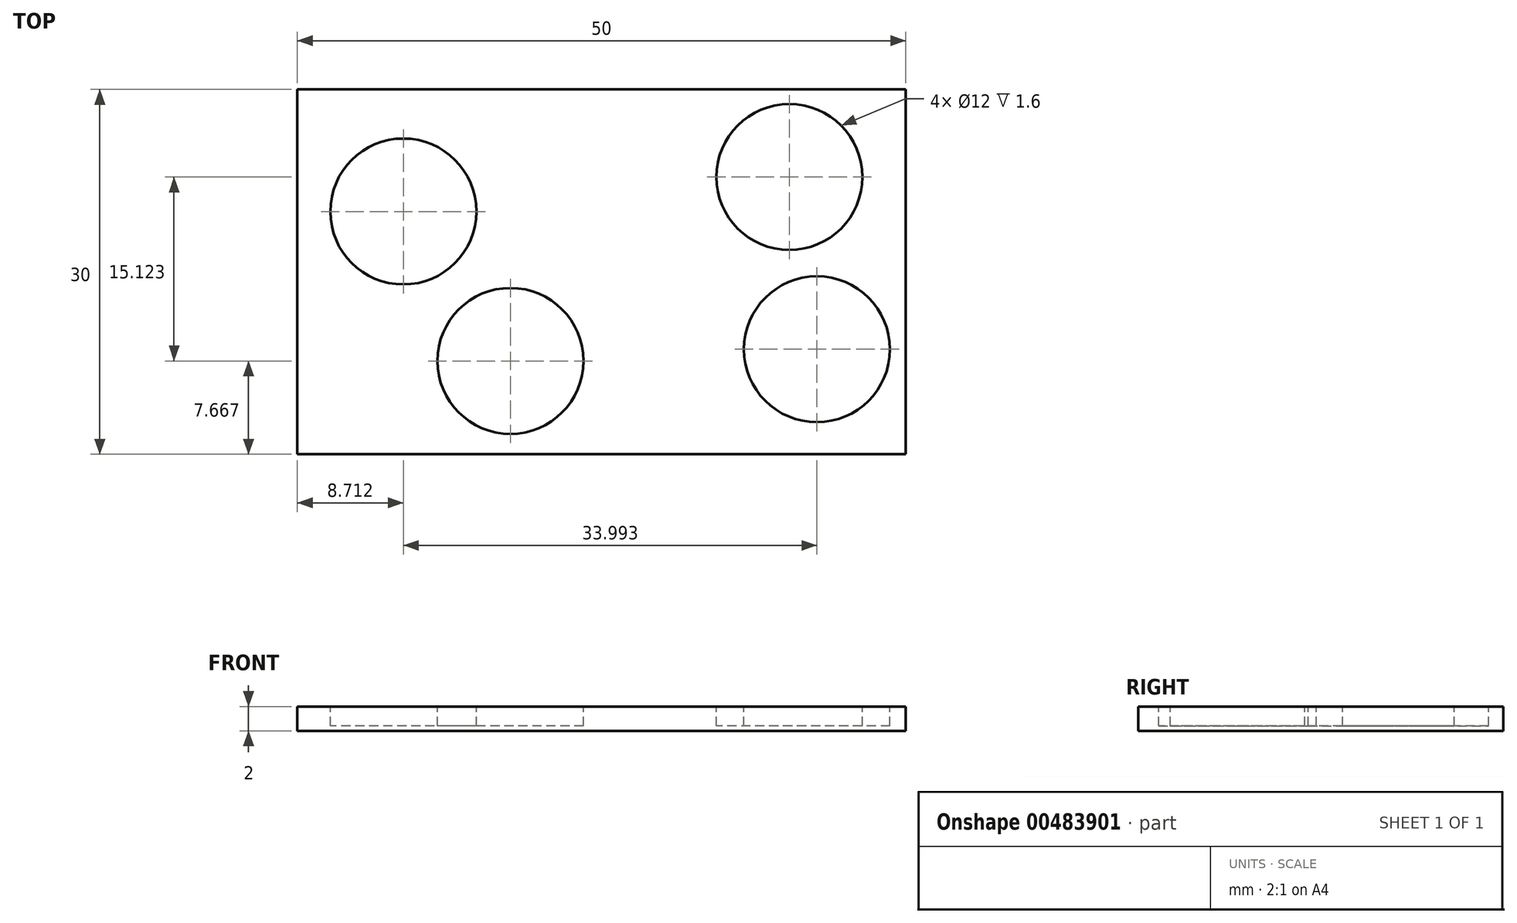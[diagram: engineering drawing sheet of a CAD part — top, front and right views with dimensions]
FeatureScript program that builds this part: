
annotation { "Feature Type Name" : "Feature", "Feature Type Description" : "" }
export const myFeature = defineFeature(function(context is Context, id is Id, definition is map)
    precondition{}
    {
        {
            var Q0;
            Q0=qCreatedBy(makeId("Top.planeOp"),FACE);
            var sketch = newSketch(context, id + "F0", { "sketchPlane" : qUnion([Q0])});
            skLineSegment(sketch, "E0.bottom", {"start": v(-25, 15) * mm, "end": v(25, 15) * mm});
            skLineSegment(sketch, "E0.top", {"start": v(-25, -15) * mm, "end": v(25, -15) * mm});
            skLineSegment(sketch, "E0.left", {"start": v(-25, 15) * mm, "end": v(-25, -15) * mm});
            skLineSegment(sketch, "E0.right", {"start": v(25, 15) * mm, "end": v(25, -15) * mm});
            skPoint(sketch, "E0.middle", {"position": v(0, 0) * mm});
            skSolve(sketch);
        }
        {
            var Q0;
            Q0=qSketchRegion(id+"F0",true);
            extrude(context, id + "F1", {"entities" : qUnion([Q0]), "oppositeDirection" : true, "depth" : 2 * mm});
        }
        {
            var Q0;
            Q0=qCreatedBy(makeId("Top.planeOp"),FACE);
            var sketch = newSketch(context, id + "F2", { "sketchPlane" : qUnion([Q0])});
            skCircle(sketch, "E1", {"center": v(-16.29, 4.96) * mm, "radius": 6 * mm});
            skCircle(sketch, "E2", {"center": v(-7.49, -7.33) * mm, "radius": 6 * mm});
            skCircle(sketch, "E3", {"center": v(15.44, 7.8) * mm, "radius": 6 * mm});
            skCircle(sketch, "E4", {"center": v(17.7, -6.37) * mm, "radius": 6 * mm});
            skSolve(sketch);
        }
        {
            var Q0;
            Q0=qSketchRegion(id+"F2",true);
            extrude(context, id + "F3", {"entities" : qUnion([Q0]), "operationType" : NewBodyOperationType.REMOVE, "oppositeDirection" : true, "depth" : 1.6 * mm});
        }
    });
